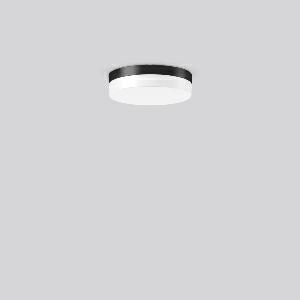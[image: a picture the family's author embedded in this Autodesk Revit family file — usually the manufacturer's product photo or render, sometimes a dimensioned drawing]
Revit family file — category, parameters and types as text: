
# Revit family: flat_slim_round_312132_0031_191_d899
name_source: partatom
category: Lighting Fixtures
units: mm (PartAtom-declared; Revit-internal decimal feet)

## family parameters
Cut with Voids When Loaded = No
Host = Face
Light Source = No
Part Type = Normal
Room Calculation Point = No
Round Connector Dimension = Use Diameter
Shared = No

## types (1)
- FLAT SLIM round (1 x LED Modul 830, 1000 lm, 3000)
    Apparent Load = 13 VA
    CIE Flux Codes = 42 72 91 89 100
    Color Rendering = 80
    Color Temperature = 3000
    Default Elevation = 1800 mm
    Height = 63 mm
    Lamp = 1 x LED Modul 830
    Lamp Light Flux = 1000 lm
    Lamp count = 1
    Length = 230 mm
    Lifetime = 50000 h
    Luminous efficacy = 77 lm/W
    Manufacturer = RZB
    ModVariant = No
    Model = 312132.0031.191
    Mounting Place = Ceiling, Wall
    Mounting Type = Surface mounted
    Number of Poles = 1
    OnlyDefault = Yes
    Power Factor = 1
    Product Name = FLAT SLIM round
    Product group = Surface mounted ceiling and wall luminaires
    ProductGroupID = 305
    Protection Class = Protection class I
    Protection Degree = IP 65
    RLX_Detail_Level = 1
    RLX_Emergency_Light_Flux = 0 lm
    RLX_Emergency_Type = 0
    RLX_Emergency_Type_DB = No
    RlxData = <blob elided: 18037 chars, md5=439b2bc0>
    Socket = socket
    Standby Power = 0 W
    System Light Flux = 1000 lm
    System Power = 13 W
    Type Comments = Product without accessories
    Type Image = 312132.0031.jpg
    URL = http://relux.com
    VarID = ---
    Voltage = 230 V
    Voltage Range = 220-240 V
    Weight = 0.00 kg
    Width = 0 mm  [stored 0 ft]

note: [stored X ft] marks values corroborated as IEEE doubles in the binary element streams (Revit-internal decimal feet)

## geometry (parser evidence)
native form markers: Blend x4, Sweep x11
no freeform markers — native parametric forms only
